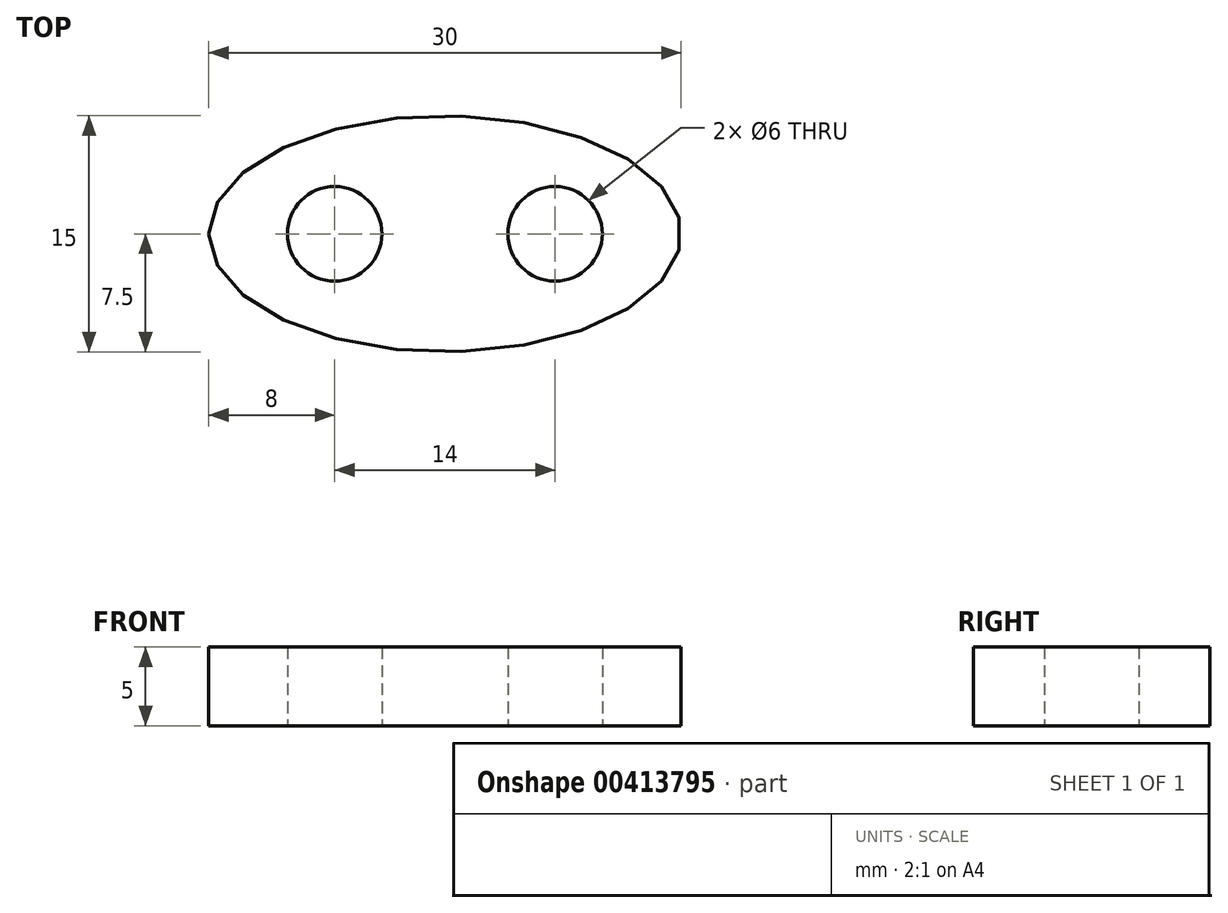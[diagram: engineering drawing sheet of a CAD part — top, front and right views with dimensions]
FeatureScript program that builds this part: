
annotation { "Feature Type Name" : "Feature", "Feature Type Description" : "" }
export const myFeature = defineFeature(function(context is Context, id is Id, definition is map)
    precondition{}
    {
        {
            var Q0;
            Q0=qCreatedBy(makeId("Top.planeOp"),FACE);
            var sketch = newSketch(context, id + "F0", { "sketchPlane" : qUnion([Q0])});
            skEllipse(sketch, "E0", {"center": v(0, 0) * mm, "majorRadius": 15 * mm, "minorRadius": 7.5 * mm, "majorAxis": v(-1, 0)});
            skCircle(sketch, "E1", {"center": v(-7, 0) * mm, "radius": 3 * mm});
            skCircle(sketch, "E2", {"center": v(7, 0) * mm, "radius": 3 * mm});
            skPoint(sketch, "E3.endSnap0", {"position": v(-15, 0) * mm});
            skPoint(sketch, "E4.middle", {"position": v(0, 7.5) * mm});
            skPoint(sketch, "E5.oppositeSnap0", {"position": v(15, 0) * mm});
            skSolve(sketch);
        }
        {
            var Q0;
            Q0=makeQuery(id+"F0.imprint","IMPRINT",FACE,{"disambiguationData":[TD([[makeQuery(id+"F0.imprint","IMPRINT",EDGE,{"derivedFrom":sQuery(id+"F0.wireOp",EDGE,"E1")}),-1.0]])]});
            var Q1;
            {var subQ0=sQuery(id+"F0.wireOp",EDGE,"yWOjGd71-whOg-qOtG-Ll9b-ojCh55xlgZNp.bottom");Q1=makeQuery(id+"F0.imprint","IMPRINT",FACE,{"disambiguationData":[TD([[makeQuery(id+"F0.imprint","IMPRINT",EDGE,{"derivedFrom":subQ0}),-1.0]])]});}
            var Q2;
            {var subQ1=sQuery(id+"F0.wireOp",EDGE,"yWOjGd71-whOg-qOtG-Ll9b-ojCh55xlgZNp.top");Q2=makeQuery(id+"F0.imprint","IMPRINT",FACE,{"disambiguationData":[TD([[makeQuery(id+"F0.imprint","IMPRINT",EDGE,{"derivedFrom":subQ1}),1.0]])]});}
            var Q3;
            {var subQ0=sQuery(id+"F0.wireOp",EDGE,"yWOjGd71-whOg-qOtG-Ll9b-ojCh55xlgZNp.right");var subQ1=sQuery(id+"F0.wireOp",EDGE,"E0");var subQ2=makeQuery(id+"F0.imprint","INTERSECT",VERTEX,{"derivedFrom":[subQ1,subQ0]});Q3=makeQuery(id+"F0.imprint","IMPRINT",FACE,{"disambiguationData":[TD([[makeQuery(id+"F0.imprint","IMPRINT",EDGE,{"disambiguationData":[TD([[subQ2,-1.0]])],"derivedFrom":subQ1}),-1.0]])]});}
            var Q4;
            {var subQ0=sQuery(id+"F0.wireOp",EDGE,"yWOjGd71-whOg-qOtG-Ll9b-ojCh55xlgZNp.left");var subQ1=sQuery(id+"F0.wireOp",EDGE,"E0");var subQ2=makeQuery(id+"F0.imprint","INTERSECT",VERTEX,{"derivedFrom":[subQ1,subQ0]});Q4=makeQuery(id+"F0.imprint","IMPRINT",FACE,{"disambiguationData":[TD([[makeQuery(id+"F0.imprint","IMPRINT",EDGE,{"disambiguationData":[TD([[subQ2,1.0]])],"derivedFrom":subQ1}),-1.0]])]});}
            var Q5;
            {var subQ1=sQuery(id+"F0.wireOp",EDGE,"yWOjGd71-whOg-qOtG-Ll9b-ojCh55xlgZNp.bottom");Q5=makeQuery(id+"F0.imprint","IMPRINT",FACE,{"disambiguationData":[TD([[makeQuery(id+"F0.imprint","IMPRINT",EDGE,{"derivedFrom":subQ1}),1.0]])]});}
            extrude(context, id + "F1", {"entities" : qUnion([Q0, Q1, Q2, Q3, Q4, Q5]), "depth" : 5 * mm});
        }
    });
